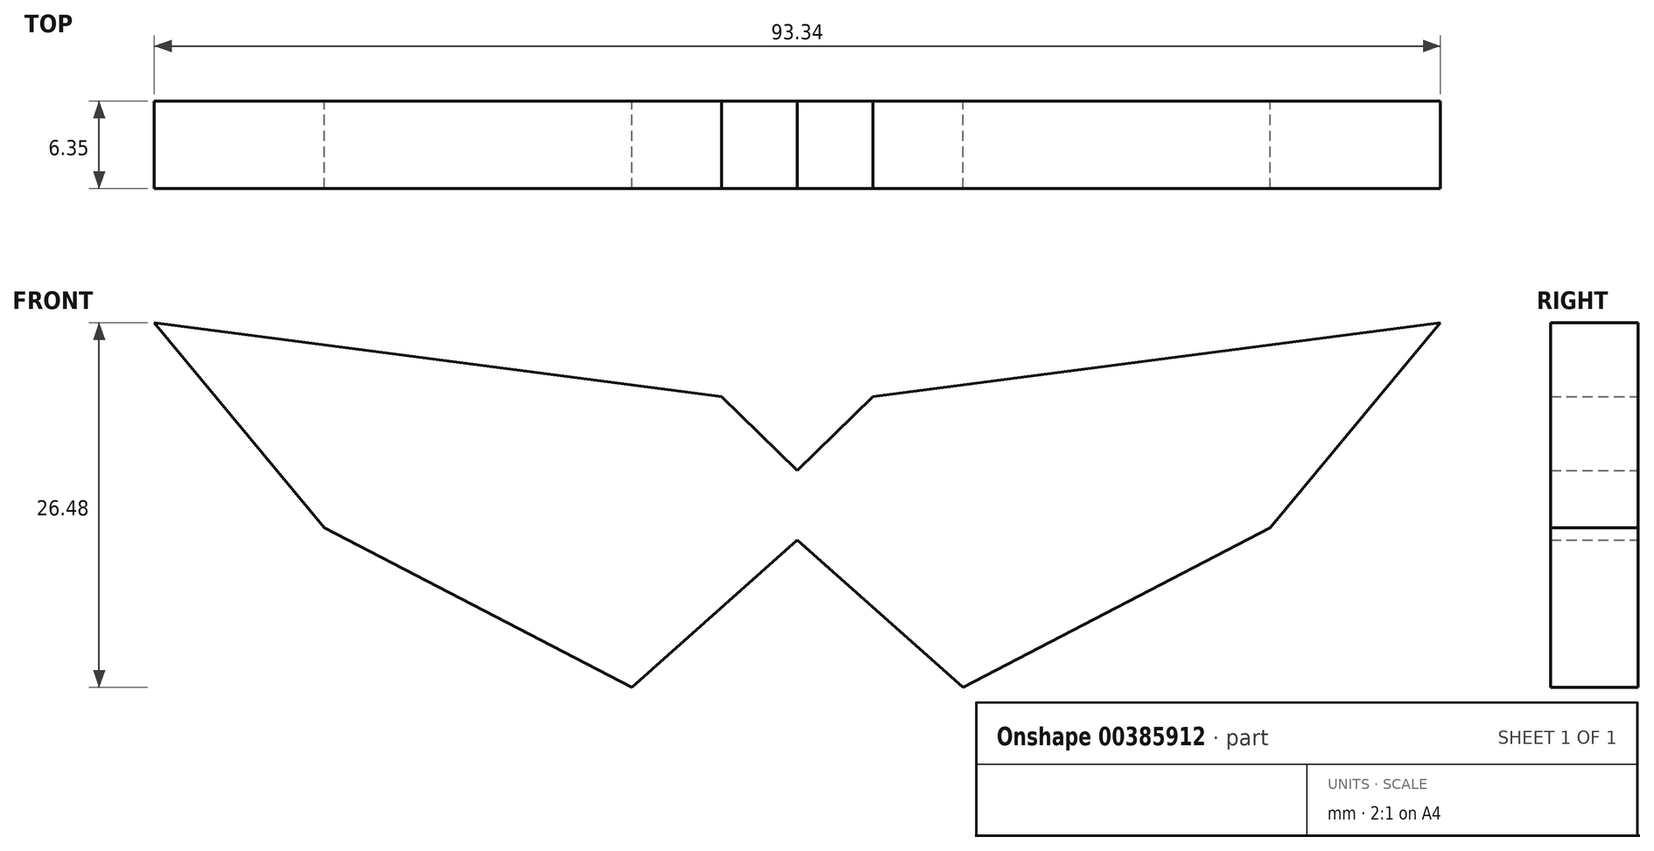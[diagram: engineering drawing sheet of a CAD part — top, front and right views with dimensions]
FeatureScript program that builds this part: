
annotation { "Feature Type Name" : "Feature", "Feature Type Description" : "" }
export const myFeature = defineFeature(function(context is Context, id is Id, definition is map)
    precondition{}
    {
        {
            var Q0;
            Q0=qCreatedBy(makeId("Front.planeOp"),FACE);
            var sketch = newSketch(context, id + "F0", { "sketchPlane" : qUnion([Q0])});
            skLineSegment(sketch, "E0", {"start": v(5.5, 5.36) * mm, "end": v(46.67, 10.73) * mm});
            skLineSegment(sketch, "E1", {"start": v(46.67, 10.73) * mm, "end": v(34.32, -4.16) * mm});
            skLineSegment(sketch, "E2", {"start": v(34.32, -4.16) * mm, "end": v(12.01, -15.75) * mm});
            skLineSegment(sketch, "E3", {"start": v(0, 0) * mm, "end": v(5.5, 5.36) * mm});
            skPoint(sketch, "E4.start.orphan", {"position": v(0, -15.75) * mm});
            skLineSegment(sketch, "E5", {"start": v(0, -5.05) * mm, "end": v(12.01, -15.75) * mm});
            skLineSegment(sketch, "E6", {"start": v(0, 0) * mm, "end": v(0, -5.05) * mm});
            skSolve(sketch);
        }
        {
            var Q0;
            Q0=makeQuery(id+"F0.imprint","IMPRINT",FACE,{"disambiguationData":[TD([[makeQuery(id+"F0.imprint","IMPRINT",EDGE,{"derivedFrom":sQuery(id+"F0.wireOp",EDGE,"E0")}),-1.0]])]});
            extrude(context, id + "F1", {"entities" : qUnion([Q0]), "depth" : 6.35 * mm});
        }
        {
            var Q0;
            Q0=makeQuery(id+"F1.opExtrude","SWEPT_BODY",BODY,{"disambiguationData":[OSD([sQuery(id+"F0.wireOp",EDGE,"E0"),sQuery(id+"F0.wireOp",EDGE,"E1"),sQuery(id+"F0.wireOp",EDGE,"E2"),sQuery(id+"F0.wireOp",EDGE,"E3"),sQuery(id+"F0.wireOp",EDGE,"E5"),sQuery(id+"F0.wireOp",EDGE,"E6")])]});
            var Q1;
            Q1=qCreatedBy(makeId("Right.planeOp"),FACE);
            mirror(context, id + "F2", {"operationType" : NewBodyOperationType.ADD, "entities" : qUnion([Q0]), "mirrorPlane" : qUnion([Q1])});
        }
    });
